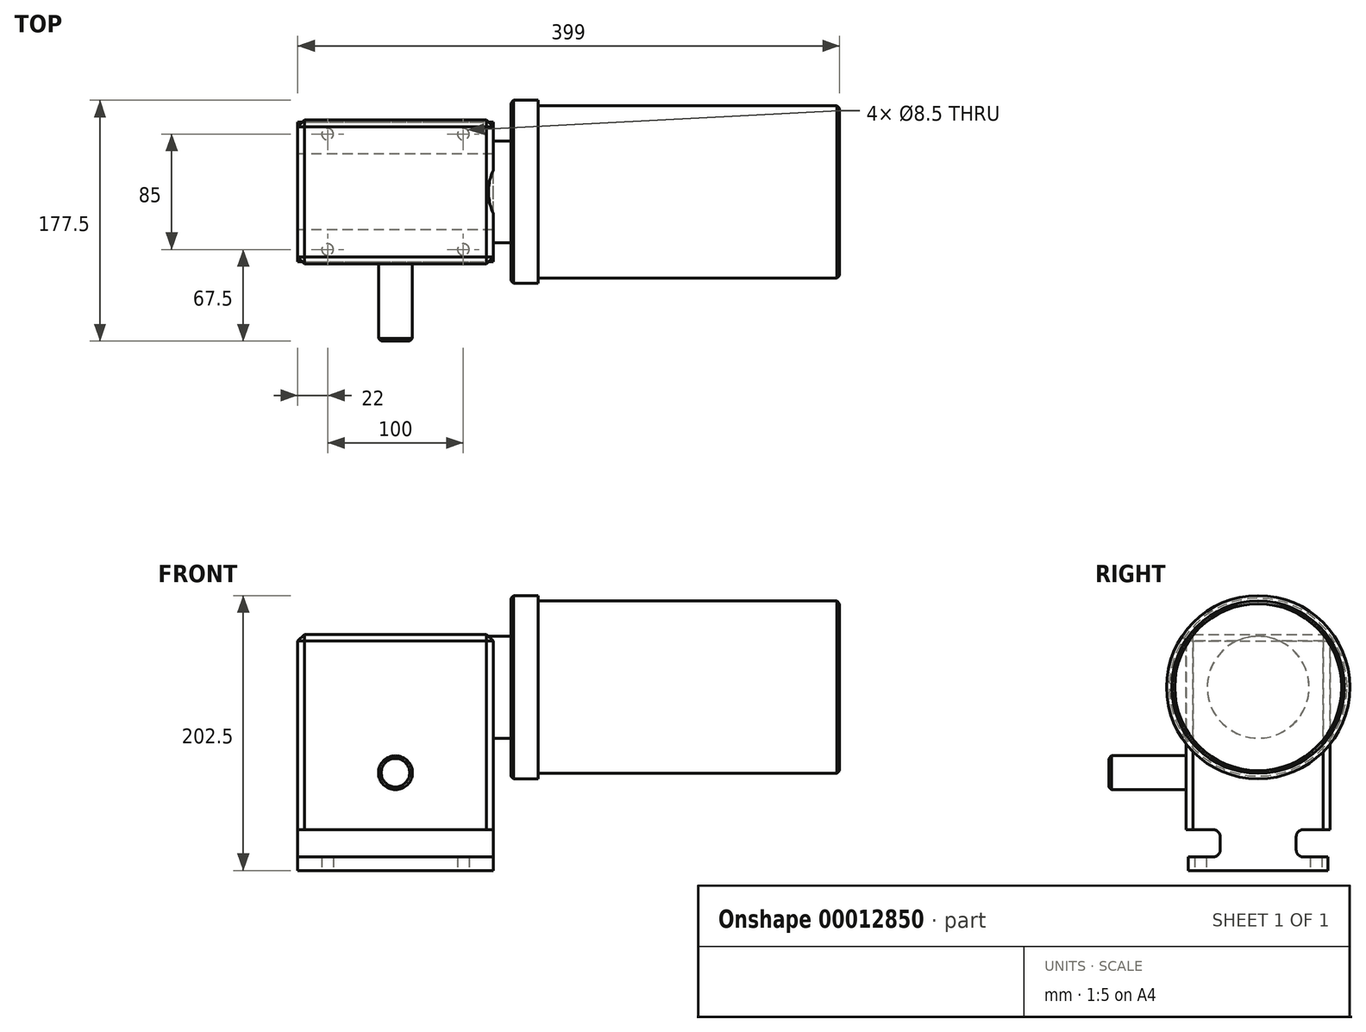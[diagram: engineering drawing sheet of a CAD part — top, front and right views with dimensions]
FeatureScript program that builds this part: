
annotation { "Feature Type Name" : "Feature", "Feature Type Description" : "" }
export const myFeature = defineFeature(function(context is Context, id is Id, definition is map)
    precondition{}
    {
        {
            var Q0;
            Q0=qCreatedBy(makeId("Front.planeOp"),FACE);
            var sketch = newSketch(context, id + "F0", { "sketchPlane" : qUnion([Q0])});
            skLineSegment(sketch, "E0.rect.bottom", {"start": v(72, 87) * mm, "end": v(-72, 87) * mm});
            skLineSegment(sketch, "E0.rect.top", {"start": v(72, -87) * mm, "end": v(-72, -87) * mm});
            skLineSegment(sketch, "E0.rect.left", {"start": v(72, 87) * mm, "end": v(72, -87) * mm});
            skLineSegment(sketch, "E0.rect.right", {"start": v(-72, 87) * mm, "end": v(-72, -87) * mm});
            skPoint(sketch, "E0.rect.middle", {"position": v(0, 0) * mm});
            skSolve(sketch);
        }
        {
            var Q0;
            Q0 = qSketchRegion(id + "F0", true);
            extrude(context, id + "F1", {"entities" : qUnion([Q0]), "depth" : 106 * mm});
        }
        {
            var Q0;
            Q0=makeQuery(id+"F1.opExtrude","CAP_FACE",FACE,{"disambiguationData":[OSD([sQuery(id+"F0.wireOp",EDGE,"E0.rect.bottom"),sQuery(id+"F0.wireOp",EDGE,"E0.rect.top"),sQuery(id+"F0.wireOp",EDGE,"E0.rect.left"),sQuery(id+"F0.wireOp",EDGE,"E0.rect.right")])],"isStart":false});
            var sketch = newSketch(context, id + "F2", { "sketchPlane" : qUnion([Q0])});
            skCircle(sketch, "E1", {"center": v(0, -15) * mm, "radius": 40 * mm, "construction": true});
            skLineSegment(sketch, "E2", {"start": v(0, 0) * mm, "end": v(0, -15) * mm, "construction": true});
            skCircle(sketch, "E3", {"center": v(0, -15) * mm, "radius": 12.5 * mm});
            skSolve(sketch);
        }
        {
            var Q0;
            Q0=makeQuery(id+"F1.opExtrude","SWEPT_FACE",FACE,{"disambiguationData":[OSD([sQuery(id+"F0.wireOp",EDGE,"E0.rect.top")])]});
            var sketch = newSketch(context, id + "F3", { "sketchPlane" : qUnion([Q0])});
            skLineSegment(sketch, "E4", {"start": v(-72, 0) * mm, "end": v(72, 106) * mm, "construction": true});
            skLineSegment(sketch, "E5.rect.bottom", {"start": v(-72, 104.5) * mm, "end": v(72, 104.5) * mm});
            skLineSegment(sketch, "E5.rect.top", {"start": v(-72, 1.5) * mm, "end": v(72, 1.5) * mm});
            skLineSegment(sketch, "E5.rect.left", {"start": v(-72, 104.5) * mm, "end": v(-72, 1.5) * mm});
            skLineSegment(sketch, "E5.rect.right", {"start": v(72, 104.5) * mm, "end": v(72, 1.5) * mm});
            skPoint(sketch, "E5.rect.middle", {"position": v(0, 53) * mm});
            skSolve(sketch);
        }
        {
            var Q0;
            {var subQ0=sQuery(id+"F3.wireOp",EDGE,"E5.rect.bottom");Q0=makeQuery(id+"F3.imprint","IMPRINT",FACE,{"disambiguationData":[TD([[makeQuery(id+"F3.imprint","IMPRINT",EDGE,{"derivedFrom":subQ0}),1.0]])]});}
            var Q1;
            {var subQ0=sQuery(id+"F3.wireOp",EDGE,"E5.rect.top");Q1=makeQuery(id+"F3.imprint","IMPRINT",FACE,{"disambiguationData":[TD([[makeQuery(id+"F3.imprint","IMPRINT",EDGE,{"derivedFrom":subQ0}),-1.0]])]});}
            extrude(context, id + "F4", {"entities" : qUnion([Q0, Q1]), "operationType" : NewBodyOperationType.REMOVE, "oppositeDirection" : true, "depth" : 10 * mm});
        }
        {
            var Q0;
            Q0=makeQuery(id+"F1.opExtrude","SWEPT_FACE",FACE,{"disambiguationData":[OSD([sQuery(id+"F0.wireOp",EDGE,"E0.rect.top")])]});
            var sketch = newSketch(context, id + "F5", { "sketchPlane" : qUnion([Q0])});
            skLineSegment(sketch, "E6", {"start": v(-72, 104.5) * mm, "end": v(72, 1.5) * mm, "construction": true});
            skLineSegment(sketch, "E7.rect.bottom", {"start": v(50, 95.5) * mm, "end": v(-50, 95.5) * mm, "construction": true});
            skLineSegment(sketch, "E7.rect.top", {"start": v(50, 10.5) * mm, "end": v(-50, 10.5) * mm, "construction": true});
            skLineSegment(sketch, "E7.rect.left", {"start": v(50, 95.5) * mm, "end": v(50, 10.5) * mm, "construction": true});
            skLineSegment(sketch, "E7.rect.right", {"start": v(-50, 95.5) * mm, "end": v(-50, 10.5) * mm, "construction": true});
            skPoint(sketch, "E7.rect.middle", {"position": v(0, 53) * mm});
            skCircle(sketch, "E8", {"center": v(-50, 95.5) * mm, "radius": 4.25 * mm});
            skCircle(sketch, "E9", {"center": v(50, 95.5) * mm, "radius": 4.25 * mm});
            skCircle(sketch, "E10", {"center": v(50, 10.5) * mm, "radius": 4.25 * mm});
            skCircle(sketch, "E11", {"center": v(-50, 10.5) * mm, "radius": 4.25 * mm});
            skSolve(sketch);
        }
        {
            var Q0;
            Q0 = qSketchRegion(id + "F5", true);
            extrude(context, id + "F6", {"entities" : qUnion([Q0]), "operationType" : NewBodyOperationType.REMOVE, "oppositeDirection" : true, "depth" : 10 * mm});
        }
        {
            var Q0;
            Q0=makeQuery(id+"F1.opExtrude","SWEPT_FACE",FACE,{"disambiguationData":[OSD([sQuery(id+"F0.wireOp",EDGE,"E0.rect.right")])]});
            var sketch = newSketch(context, id + "F7", { "sketchPlane" : qUnion([Q0])});
            skLineSegment(sketch, "E12.bottom", {"start": v(0, -77) * mm, "end": v(25, -77) * mm});
            skLineSegment(sketch, "E12.top", {"start": v(0, -57) * mm, "end": v(25, -57) * mm});
            skLineSegment(sketch, "E12.left", {"start": v(0, -77) * mm, "end": v(0, -57) * mm});
            skLineSegment(sketch, "E12.right", {"start": v(25, -77) * mm, "end": v(25, -57) * mm});
            skLineSegment(sketch, "E13", {"start": v(53, -87) * mm, "end": v(53, 87) * mm, "construction": true});
            skLineSegment(sketch, "E14.MirrorCS", {"start": v(81, -77) * mm, "end": v(81, -57) * mm});
            skLineSegment(sketch, "E15.MirrorCS", {"start": v(106, -57) * mm, "end": v(81, -57) * mm});
            skLineSegment(sketch, "E16.MirrorCS", {"start": v(106, -77) * mm, "end": v(106, -57) * mm});
            skLineSegment(sketch, "E17.MirrorCS", {"start": v(106, -77) * mm, "end": v(81, -77) * mm});
            skSolve(sketch);
        }
        {
            var Q0;
            Q0 = qSketchRegion(id + "F7", true);
            extrude(context, id + "F8", {"entities" : qUnion([Q0]), "operationType" : NewBodyOperationType.REMOVE, "endBound" : BoundingType.THROUGH_ALL, "oppositeDirection" : true, "depth" : 25 * mm});
        }
        {
            var Q0;
            Q0=qCreatedBy(makeId("Right.planeOp"),FACE);
            cPlane(context, id + "F9", {"entities" : qUnion([Q0]), "cplaneType" : CPlaneType.OFFSET, "offset" : 95 * mm, "width" : 150 * mm, "height" : 150 * mm});
        }
        {
            var Q0;
            Q0=qCreatedBy(id+"F9.planeOp",FACE);
            var sketch = newSketch(context, id + "F10", { "sketchPlane" : qUnion([Q0])});
            skLineSegment(sketch, "E18.0", {"start": v(-104.5, -87) * mm, "end": v(-1.5, -87) * mm, "construction": true});
            skLineSegment(sketch, "E19", {"start": v(-53, -87) * mm, "end": v(-53, 83.36) * mm, "construction": true});
            skCircle(sketch, "E20", {"center": v(-53, 48) * mm, "radius": 67.5 * mm});
            skSolve(sketch);
        }
        {
            var Q0;
            Q0 = qSketchRegion(id + "F10", true);
            extrude(context, id + "F11", {"entities" : qUnion([Q0]), "operationType" : NewBodyOperationType.ADD, "oppositeDirection" : true, "depth" : 10 * mm});
        }
        {
            var Q0;
            Q0=makeQuery(id+"F11.opExtrude","CAP_FACE",FACE,{"disambiguationData":[OSD([sQuery(id+"F10.wireOp",EDGE,"E20")])],"isStart":false});
            var sketch = newSketch(context, id + "F12", { "sketchPlane" : qUnion([Q0])});
            skCircle(sketch, "E21", {"center": v(53, 48) * mm, "radius": 37.5 * mm});
            skSolve(sketch);
        }
        {
            var Q0;
            Q0 = qSketchRegion(id + "F12", true);
            extrude(context, id + "F13", {"entities" : qUnion([Q0]), "operationType" : NewBodyOperationType.ADD, "endBound" : BoundingType.UP_TO_NEXT, "depth" : 25 * mm});
        }
        {
            var Q0;
            Q0=makeQuery(id+"F11.opExtrude","CAP_FACE",FACE,{"disambiguationData":[OSD([sQuery(id+"F10.wireOp",EDGE,"E20")])],"isStart":true});
            var sketch = newSketch(context, id + "F14", { "sketchPlane" : qUnion([Q0])});
            skCircle(sketch, "E22.0", {"center": v(-53, 48) * mm, "radius": 67.5 * mm});
            skSolve(sketch);
        }
        {
            var Q0;
            Q0 = qSketchRegion(id + "F14", true);
            extrude(context, id + "F15", {"entities" : qUnion([Q0]), "operationType" : NewBodyOperationType.ADD, "depth" : 10 * mm});
        }
        {
            var Q0;
            Q0=makeQuery(id+"F15.opExtrude","CAP_FACE",FACE,{"disambiguationData":[OSD([sQuery(id+"F14.wireOp",EDGE,"E22.0")])],"isStart":false});
            var sketch = newSketch(context, id + "F16", { "sketchPlane" : qUnion([Q0])});
            skCircle(sketch, "E23", {"center": v(-53, 48) * mm, "radius": 63.5 * mm});
            skSolve(sketch);
        }
        {
            var Q0;
            Q0 = qSketchRegion(id + "F16", true);
            extrude(context, id + "F17", {"entities" : qUnion([Q0]), "operationType" : NewBodyOperationType.ADD, "depth" : 222 * mm});
        }
        {
            var Q0;
            Q0 = qSketchRegion(id + "F2", true);
            extrude(context, id + "F18", {"entities" : qUnion([Q0]), "operationType" : NewBodyOperationType.ADD, "depth" : 57 * mm});
        }
        {
            var Q0;
            Q0=makeQuery(id+"F18.opExtrude","CAP_EDGE",EDGE,{"disambiguationData":[OSD([sQuery(id+"F2.wireOp",EDGE,"E3")])],"isStart":false});
            var Q1;
            Q1=makeQuery(id+"F17.opExtrude","CAP_EDGE",EDGE,{"disambiguationData":[OSD([sQuery(id+"F16.wireOp",EDGE,"E23")])],"isStart":false});
            var Q2;
            Q2=makeQuery(id+"F11.opExtrude","CAP_EDGE",EDGE,{"disambiguationData":[OSD([sQuery(id+"F10.wireOp",EDGE,"E20")])],"isStart":false});
            chamfer(context, id + "F19", {"entities" : qUnion([Q0, Q1, Q2]), "width" : 2 * mm, "tangentPropagation" : true});
        }
        {
            var Q0;
            Q0=makeQuery(id+"F1.opExtrude","SWEPT_EDGE",EDGE,{"disambiguationData":[OSD([sQuery(id+"F0.wireOp",EDGE,"E0.rect.bottom"),sQuery(id+"F0.wireOp",EDGE,"E0.rect.right")])]});
            var Q1;
            Q1=makeQuery(id+"F1.opExtrude","SWEPT_EDGE",EDGE,{"disambiguationData":[OSD([sQuery(id+"F0.wireOp",EDGE,"E0.rect.bottom"),sQuery(id+"F0.wireOp",EDGE,"E0.rect.left")])]});
            var Q2;
            Q2=makeQuery(id+"F1.opExtrude","CAP_EDGE",EDGE,{"disambiguationData":[OSD([sQuery(id+"F0.wireOp",EDGE,"E0.rect.right")])],"isStart":false});
            var Q3;
            Q3=makeQuery(id+"F1.opExtrude","CAP_EDGE",EDGE,{"disambiguationData":[OSD([sQuery(id+"F0.wireOp",EDGE,"E0.rect.right")])],"isStart":true});
            var Q4;
            Q4=makeQuery(id+"F1.opExtrude","CAP_EDGE",EDGE,{"disambiguationData":[OSD([sQuery(id+"F0.wireOp",EDGE,"E0.rect.left")])],"isStart":false});
            var Q5;
            Q5=makeQuery(id+"F1.opExtrude","CAP_EDGE",EDGE,{"disambiguationData":[OSD([sQuery(id+"F0.wireOp",EDGE,"E0.rect.left")])],"isStart":true});
            var Q6;
            Q6=makeQuery(id+"F1.opExtrude","CAP_EDGE",EDGE,{"disambiguationData":[OSD([sQuery(id+"F0.wireOp",EDGE,"E0.rect.bottom")])],"isStart":false});
            var Q7;
            Q7=makeQuery(id+"F1.opExtrude","CAP_EDGE",EDGE,{"disambiguationData":[OSD([sQuery(id+"F0.wireOp",EDGE,"E0.rect.bottom")])],"isStart":true});
            chamfer(context, id + "F20", {"entities" : qUnion([Q0, Q1, Q2, Q3, Q4, Q5, Q6, Q7]), "width" : 5 * mm, "tangentPropagation" : true});
        }
        {
            var Q0;
            Q0=makeQuery(id+"F8.boolean.opBoolean","COPY",EDGE,{"derivedFrom":makeQuery(id+"F8.opExtrude","SWEPT_EDGE",EDGE,{"disambiguationData":[OSD([sQuery(id+"F7.wireOp",EDGE,"E14.MirrorCS"),sQuery(id+"F7.wireOp",EDGE,"E15.MirrorCS")])]})});
            var Q1;
            Q1=makeQuery(id+"F8.boolean.opBoolean","COPY",EDGE,{"derivedFrom":makeQuery(id+"F8.opExtrude","SWEPT_EDGE",EDGE,{"disambiguationData":[OSD([sQuery(id+"F7.wireOp",EDGE,"E14.MirrorCS"),sQuery(id+"F7.wireOp",EDGE,"E17.MirrorCS")])]})});
            var Q2;
            Q2=makeQuery(id+"F8.boolean.opBoolean","COPY",EDGE,{"derivedFrom":makeQuery(id+"F8.opExtrude","SWEPT_EDGE",EDGE,{"disambiguationData":[OSD([sQuery(id+"F7.wireOp",EDGE,"E12.top"),sQuery(id+"F7.wireOp",EDGE,"E12.right")])]})});
            var Q3;
            Q3=makeQuery(id+"F8.boolean.opBoolean","COPY",EDGE,{"derivedFrom":makeQuery(id+"F8.opExtrude","SWEPT_EDGE",EDGE,{"disambiguationData":[OSD([sQuery(id+"F7.wireOp",EDGE,"E12.bottom"),sQuery(id+"F7.wireOp",EDGE,"E12.right")])]})});
            fillet(context, id + "F21", {"entities" : qUnion([Q0, Q1, Q2, Q3]), "radius" : 5 * mm, "tangentPropagation" : true, "allowEdgeOverflow" : false});
        }
    });
